# Revit family: ge-u722_60Hz
name_source: partatom
category: 衛生器具
units: mm (PartAtom-declared; Revit-internal decimal feet)

## family parameters
OmniClass タイトル = Heat Pumps, Heating Function
OmniClass 番号 = 23.75.10.17.17.11
パーツ タイプ = 標準
ロード時にボイドで切り取り = いいえ
丸型コネクタ寸法 = 直径を使用
作業面ベース = いいえ
共有 = いいえ
常に垂直 = はい
部屋計算ポイント = いいえ

## types (2) — shared parameters
Clearance Back = 100  [stored 0.328084 ft]
Clearance Front = 300
Clearance Left = 150
Clearance Right = 300
Clearance Top = 1000  [stored 3.28084 ft]
Depth = 300
FamilyVersion = ver1.6
Height = 715  [stored 2.3458 ft]
IfcExportAs = IfcPumpType
IfcExportType = USERDEFINED
OmniClassCode = 23-33 17 11 11
URL = https://www.mitsubishielectric.co.jp
Uniclass2015Code = Pr_70_60_37_04
Uniclass2015Title = Air to water heat pumps
Uniclass2015Version = Systems v1.9
Width = 879  [stored 2.88386 ft]
ケーブルサイズ = 0 mm
サービススペース = はい
ヒートポンプユニット運転音 中間期標準 （dB(A)) = 44
ヒートポンプユニット運転音 冬期標準 （dB(A)) = 47
ヒートポンプユニット運転音 冬期高温 （dB(A)) = 47
ユニット数 = 1
上水管径 = 0 mm
上水量 = 0.0 L
仕様書バージョン = Version1.0
企業コード = 108420
分類コード = 50056502300030
参照している仕様書等のバージョン = 公共建築工事標準仕様書（機械設備工事編）平成31年度版
吊り位置X = 500  [stored 1.64042 ft]
吊り位置Y = 330
周波数 = 60 Hz
呼称 = ヒートポンプ給湯機
形式 = 業務用ヒートポンプ給湯機
排気配管 = いいえ
排水管径 = 16 mm
排水配管 = いいえ
推奨ブレーカー容量 = 0 A
最大電流値 = 0 A
最高使用圧力 = 0.0 Pa
最高給水圧力 = 0 kPa
極数 = 3
水配管 = いいえ
沸き上げ温度範囲 = 約65～85℃
法定耐用年数 = 15
消費電力 = 1.67 kW
減圧弁圧力 = 0.0 Pa
温水入口温度_一次側 = 0 °C
温水出口温度_一次側 = 0 °C
温水配管 = いいえ
積算_科目 = 8 給湯設備
符号 = WHP
給湯管径 = 0 mm
給湯能力 = 7.20 kW
製品リリース年月 = 2015/02/27
製品出荷対象 = 国内
製造元 = 三菱電機株式会社
設置方法 = 床置
説明 = 自然冷媒CO２小型業務用ヒートポンプ給湯機
負荷分類 = 1_熱源類
貯湯量 = 0.0 L
質量 = 0.00 kg
電動機出力_圧縮機 = 1.30 kW
電動機出力_送風機 = 0.05 kW
電圧 = 0 V
電圧_補機 = 0 V
電源種別 = 一般
騒音レベル(dB(A)) = 47
zero-valued in all types: Clearance Bottom, S寸法, 価格, 機械基礎_D, 機械基礎_H, 機械基礎_W, 機械基礎質量, 耐震強度

## per-type parameters (varying)
| type | 構成品番 | 製品質量 | 運転質量 |
| ヒートポンプユニット_GE-U722S_三相 | GE-U722S | 53.00 kg | 53.00 kg |
| ヒートポンプユニット_GE-U722_単相 | GE-U722 | 55.00 kg | 55.00 kg |

note: [stored X ft] marks values corroborated as IEEE doubles in the binary element streams (Revit-internal decimal feet)
